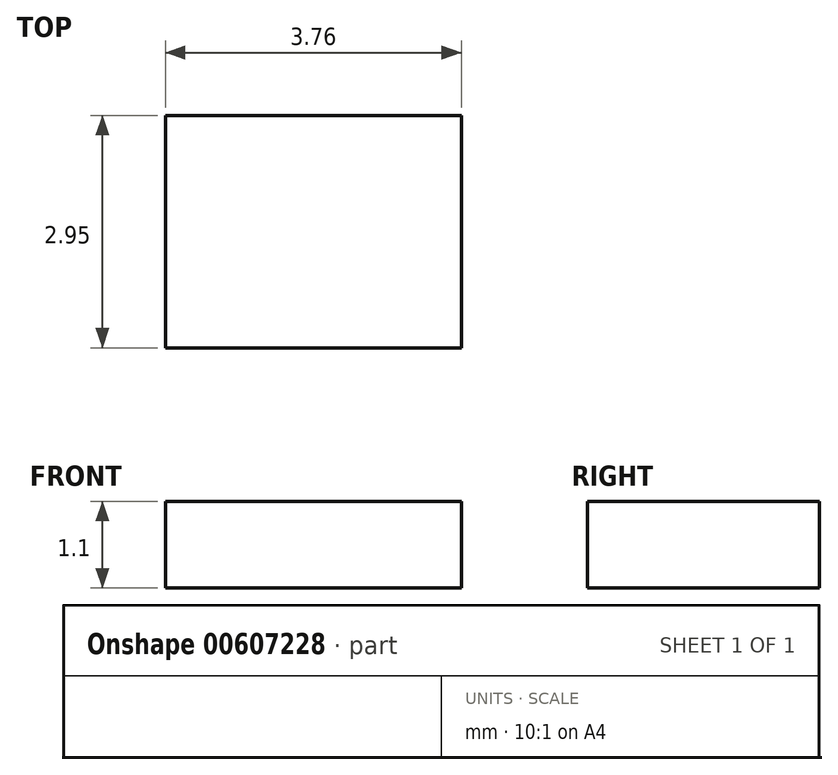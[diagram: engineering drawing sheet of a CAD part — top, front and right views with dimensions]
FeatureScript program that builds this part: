
annotation { "Feature Type Name" : "Feature", "Feature Type Description" : "" }
export const myFeature = defineFeature(function(context is Context, id is Id, definition is map)
    precondition{}
    {
        {
            var Q0;
            Q0=qCreatedBy(makeId("Front.planeOp"),FACE);
            var sketch = newSketch(context, id + "F0", { "sketchPlane" : qUnion([Q0])});
            skLineSegment(sketch, "E0.bottom", {"start": v(0, 0) * mm, "end": v(3.76, 0) * mm});
            skLineSegment(sketch, "E0.top", {"start": v(0, 1.1) * mm, "end": v(3.76, 1.1) * mm});
            skLineSegment(sketch, "E0.left", {"start": v(0, 0) * mm, "end": v(0, 1.1) * mm});
            skLineSegment(sketch, "E0.right", {"start": v(3.76, 0) * mm, "end": v(3.76, 1.1) * mm});
            skSolve(sketch);
        }
        {
            var Q0;
            Q0=makeQuery(id+"F0.imprint","IMPRINT",FACE,{"disambiguationData":[TD([[makeQuery(id+"F0.imprint","IMPRINT",EDGE,{"derivedFrom":sQuery(id+"F0.wireOp",EDGE,"E0.bottom")}),1.0]])]});
            extrude(context, id + "F1", {"entities" : qUnion([Q0]), "depth" : 2.95 * mm, "offsetDistance" : 25.4 * mm});
        }
    });
